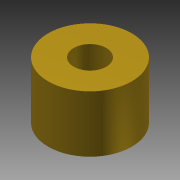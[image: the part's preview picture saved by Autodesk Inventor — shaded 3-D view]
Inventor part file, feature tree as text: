
AUTODESK INVENTOR PART (.ipt)
format: ipt  version: 2016 (Build 200138000, 138)  size: 82,432 bytes
history: native  units: in
note: dims shown in document units (in); Inventor stores cm internally (conversion verified against a paired STEP export)
features: other x2, sketch x1, imported_body x1
ambient origin geometry x8: Origin, YZ Plane, XZ Plane, XY Plane, X Axis, Y Axis, Z Axis, Center Point
bodies: Body1 (feature_tree)
feature tree (4):
  other  "Boss-Extrude1"
  other  "shaft.ipt1"
  sketch  "Sketch1"
  imported_body  "Base1"
